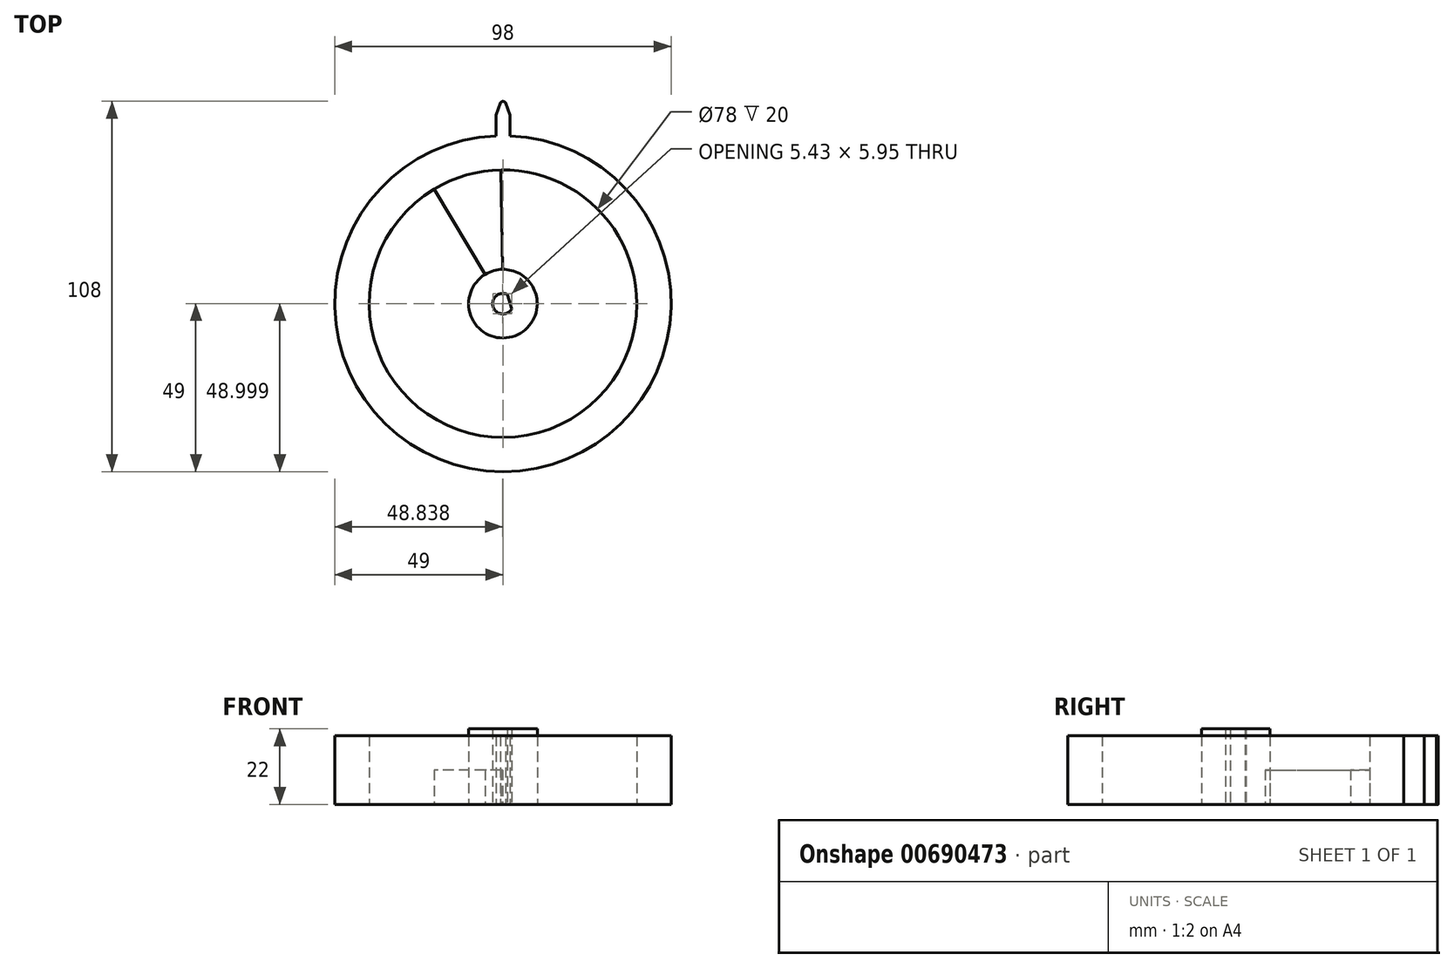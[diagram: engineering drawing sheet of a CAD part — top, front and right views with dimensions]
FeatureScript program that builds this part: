
annotation { "Feature Type Name" : "Feature", "Feature Type Description" : "" }
export const myFeature = defineFeature(function(context is Context, id is Id, definition is map)
    precondition{}
    {
        {
            var Q0;
            Q0=qCreatedBy(makeId("Top.planeOp"),FACE);
            var sketch = newSketch(context, id + "F0", { "sketchPlane" : qUnion([Q0])});
            skCircle(sketch, "E0", {"center": v(0, 0) * mm, "radius": 49 * mm});
            skCircle(sketch, "E1", {"center": v(0, 0) * mm, "radius": 39 * mm});
            skCircle(sketch, "E2", {"center": v(0, 0) * mm, "radius": 10 * mm});
            skCircle(sketch, "E3", {"center": v(0, 0) * mm, "radius": 3 * mm});
            skLineSegment(sketch, "E4", {"start": v(1.28, 2.71) * mm, "end": v(2.55, -1.57) * mm});
            skLineSegment(sketch, "E5", {"start": v(0, 49) * mm, "end": v(0, 59) * mm});
            skLineSegment(sketch, "E6", {"start": v(0, 59) * mm, "end": v(2, 59) * mm});
            skLineSegment(sketch, "E7", {"start": v(2, 59) * mm, "end": v(2, 48.96) * mm});
            skLineSegment(sketch, "E8", {"start": v(0, 59) * mm, "end": v(-2, 59) * mm});
            skLineSegment(sketch, "E9", {"start": v(-2, 59) * mm, "end": v(-2, 48.96) * mm});
            skLineSegment(sketch, "E10", {"start": v(0, 0) * mm, "end": v(-20.08, 33.43) * mm});
            skLineSegment(sketch, "E11", {"start": v(0, 0) * mm, "end": v(-0.68, 39) * mm});
            skLineSegment(sketch, "E12", {"start": v(0.62, 59) * mm, "end": v(2, 54.94) * mm});
            skArc(sketch, "E13", {"start": v(0, 59) * mm, "mid": v(0.54, 58.81) * mm, "end": v(0.85, 58.33) * mm});
            skLineSegment(sketch, "E14.MirrorCS", {"start": v(-0.62, 59) * mm, "end": v(-2, 54.94) * mm});
            skArc(sketch, "E15.MirrorCS", {"start": v(0, 59) * mm, "mid": v(-0.54, 58.81) * mm, "end": v(-0.85, 58.33) * mm});
            skSolve(sketch);
        }
        {
            var Q0;
            {var subQ3=sQuery(id+"F0.wireOp",EDGE,"E0");var subQ6=makeQuery(id+"F0.imprint","INTERSECT",VERTEX,{"derivedFrom":[subQ3,sQuery(id+"F0.wireOp",EDGE,"E5")]});Q0=makeQuery(id+"F0.imprint","IMPRINT",FACE,{"disambiguationData":[TD([[makeQuery(id+"F0.imprint","IMPRINT",EDGE,{"disambiguationData":[TD([[subQ6,1.0]])],"derivedFrom":subQ3}),1.0]])]});}
            extrude(context, id + "F1", {"entities" : qUnion([Q0]), "depth" : 20 * mm, "offsetDistance" : 25 * mm});
        }
        {
            var Q0;
            {var subQ0=sQuery(id+"F0.wireOp",EDGE,"E5");Q0=makeQuery(id+"F0.imprint","IMPRINT",FACE,{"disambiguationData":[TD([[makeQuery(id+"F0.imprint","IMPRINT",EDGE,{"derivedFrom":subQ0}),-1.0]])]});}
            var Q1;
            {var subQ5=sQuery(id+"F0.wireOp",EDGE,"E5");Q1=makeQuery(id+"F0.imprint","IMPRINT",FACE,{"disambiguationData":[TD([[makeQuery(id+"F0.imprint","IMPRINT",EDGE,{"derivedFrom":subQ5}),1.0]])]});}
            extrude(context, id + "F2", {"entities" : qUnion([Q0, Q1]), "operationType" : NewBodyOperationType.ADD, "depth" : 20 * mm, "offsetDistance" : 25 * mm});
        }
        {
            var Q0;
            {var subQ0=sQuery(id+"F0.wireOp",EDGE,"E10");var subQ1=sQuery(id+"F0.wireOp",EDGE,"E1");var subQ2=makeQuery(id+"F0.imprint","INTERSECT",VERTEX,{"derivedFrom":[subQ1,subQ0]});Q0=makeQuery(id+"F0.imprint","IMPRINT",FACE,{"disambiguationData":[TD([[makeQuery(id+"F0.imprint","IMPRINT",EDGE,{"disambiguationData":[TD([[subQ2,1.0]])],"derivedFrom":subQ1}),1.0]])]});}
            extrude(context, id + "F3", {"entities" : qUnion([Q0]), "operationType" : NewBodyOperationType.ADD, "depth" : 10 * mm, "offsetDistance" : 25 * mm});
        }
        {
            var Q0;
            {var subQ4=sQuery(id+"F0.wireOp",EDGE,"E10");var subQ6=sQuery(id+"F0.wireOp",EDGE,"E2");var subQ7=makeQuery(id+"F0.imprint","INTERSECT",VERTEX,{"derivedFrom":[subQ6,subQ4]});Q0=makeQuery(id+"F0.imprint","IMPRINT",FACE,{"disambiguationData":[TD([[makeQuery(id+"F0.imprint","IMPRINT",EDGE,{"disambiguationData":[TD([[subQ7,-1.0]])],"derivedFrom":subQ6}),1.0]])]});}
            var Q1;
            {var subQ0=sQuery(id+"F0.wireOp",EDGE,"E10");var subQ1=sQuery(id+"F0.wireOp",EDGE,"E2");var subQ2=makeQuery(id+"F0.imprint","INTERSECT",VERTEX,{"derivedFrom":[subQ1,subQ0]});Q1=makeQuery(id+"F0.imprint","IMPRINT",FACE,{"disambiguationData":[TD([[makeQuery(id+"F0.imprint","IMPRINT",EDGE,{"disambiguationData":[TD([[subQ2,1.0]])],"derivedFrom":subQ1}),1.0]])]});}
            var Q2;
            {var subQ0=sQuery(id+"F0.wireOp",EDGE,"E4");Q2=makeQuery(id+"F0.imprint","IMPRINT",FACE,{"disambiguationData":[TD([[makeQuery(id+"F0.imprint","IMPRINT",EDGE,{"derivedFrom":subQ0}),1.0]])]});}
            extrude(context, id + "F4", {"entities" : qUnion([Q0, Q1, Q2]), "operationType" : NewBodyOperationType.ADD, "depth" : 22 * mm, "offsetDistance" : 25 * mm});
        }
    });
